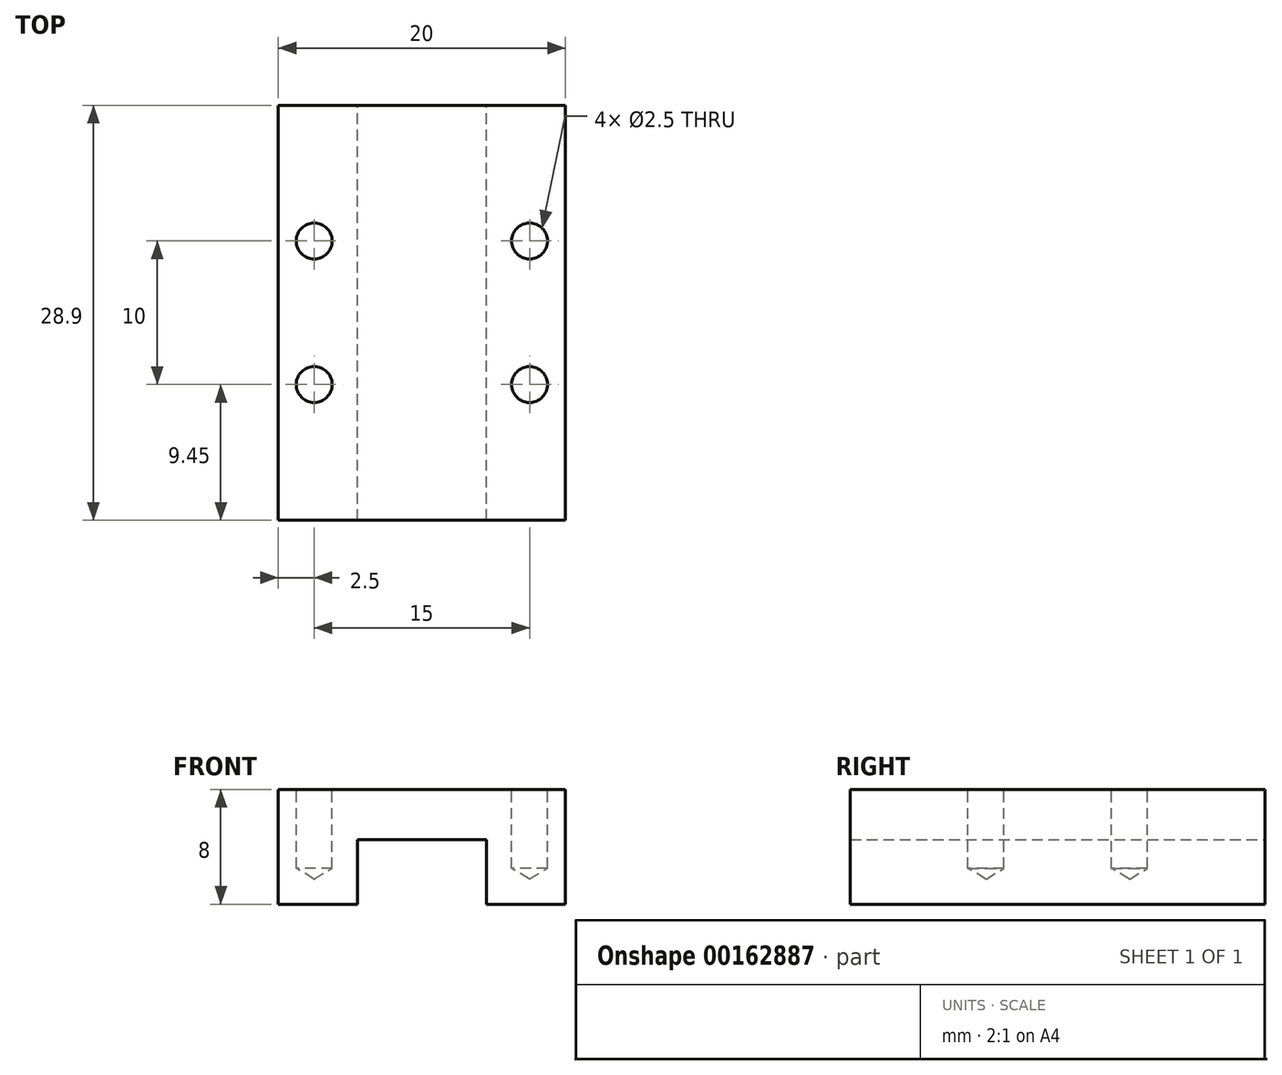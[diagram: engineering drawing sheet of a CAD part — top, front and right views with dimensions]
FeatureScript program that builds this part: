
annotation { "Feature Type Name" : "Feature", "Feature Type Description" : "" }
export const myFeature = defineFeature(function(context is Context, id is Id, definition is map)
    precondition{}
    {
        {
            var Q0;
            Q0=qCreatedBy(makeId("Front.planeOp"),FACE);
            var sketch = newSketch(context, id + "F0", { "sketchPlane" : qUnion([Q0])});
            skLineSegment(sketch, "E0", {"start": v(0, 4.05) * mm, "end": v(-10, 4.05) * mm});
            skLineSegment(sketch, "E1", {"start": v(-10, 4.05) * mm, "end": v(-10, -3.95) * mm});
            skLineSegment(sketch, "E2", {"start": v(-10, -3.95) * mm, "end": v(-4.5, -3.95) * mm});
            skLineSegment(sketch, "E3", {"start": v(-4.5, -3.95) * mm, "end": v(-4.5, 0.55) * mm});
            skLineSegment(sketch, "E4", {"start": v(-4.5, 0.55) * mm, "end": v(0, 0.55) * mm});
            skLineSegment(sketch, "E5.MirrorCS", {"start": v(4.5, -3.95) * mm, "end": v(4.5, 0.55) * mm});
            skLineSegment(sketch, "E6.MirrorCS", {"start": v(0, 4.05) * mm, "end": v(10, 4.05) * mm});
            skLineSegment(sketch, "E7.MirrorCS", {"start": v(10, -3.95) * mm, "end": v(4.5, -3.95) * mm});
            skLineSegment(sketch, "E8.MirrorCS", {"start": v(4.5, 0.55) * mm, "end": v(0, 0.55) * mm});
            skLineSegment(sketch, "E9.MirrorCS", {"start": v(10, 4.05) * mm, "end": v(10, -3.95) * mm});
            skSolve(sketch);
        }
        {
            var Q0;
            Q0=makeQuery(id+"F0.imprint","IMPRINT",FACE,{"disambiguationData":[TD([[makeQuery(id+"F0.imprint","IMPRINT",EDGE,{"derivedFrom":sQuery(id+"F0.wireOp",EDGE,"E0")}),1.0]])]});
            extrude(context, id + "F1", {"entities" : qUnion([Q0]), "depth" : 14.45 * mm, "offsetDistance" : 25 * mm, "hasSecondDirection" : true, "secondDirectionOppositeDirection" : true, "secondDirectionDepth" : 14.45 * mm});
        }
        {
            var Q0;
            Q0=makeQuery(id+"F1.opExtrude","SWEPT_FACE",FACE,{"disambiguationData":[OSD([sQuery(id+"F0.wireOp",EDGE,"E0"),sQuery(id+"F0.wireOp",EDGE,"E6.MirrorCS")])]});
            var sketch = newSketch(context, id + "F2", { "sketchPlane" : qUnion([Q0])});
            skLineSegment(sketch, "E10.bottom", {"start": v(7.5, -5) * mm, "end": v(-7.5, -5) * mm, "construction": true});
            skLineSegment(sketch, "E10.top", {"start": v(7.5, 5) * mm, "end": v(-7.5, 5) * mm, "construction": true});
            skLineSegment(sketch, "E10.left", {"start": v(7.5, -5) * mm, "end": v(7.5, 5) * mm, "construction": true});
            skLineSegment(sketch, "E10.right", {"start": v(-7.5, -5) * mm, "end": v(-7.5, 5) * mm, "construction": true});
            skPoint(sketch, "E10.middle", {"position": v(0, 0) * mm});
            skSolve(sketch);
        }
        {
            var Q0;
            Q0=sQuery(id+"F2.wireOp",VERTEX,"E10.top.end");
            var Q1;
            Q1=sQuery(id+"F2.wireOp",VERTEX,"E10.bottom.end");
            var Q2;
            Q2=sQuery(id+"F2.wireOp",VERTEX,"E10.bottom.start");
            var Q3;
            Q3=sQuery(id+"F2.wireOp",VERTEX,"E10.top.start");
            var Q4;
            Q4=makeQuery(id+"F1.opExtrude","SWEPT_BODY",BODY,{"disambiguationData":[OSD([sQuery(id+"F0.wireOp",EDGE,"E0"),sQuery(id+"F0.wireOp",EDGE,"E1"),sQuery(id+"F0.wireOp",EDGE,"E2"),sQuery(id+"F0.wireOp",EDGE,"E3"),sQuery(id+"F0.wireOp",EDGE,"E4"),sQuery(id+"F0.wireOp",EDGE,"E5.MirrorCS"),sQuery(id+"F0.wireOp",EDGE,"E6.MirrorCS"),sQuery(id+"F0.wireOp",EDGE,"E7.MirrorCS"),sQuery(id+"F0.wireOp",EDGE,"E8.MirrorCS"),sQuery(id+"F0.wireOp",EDGE,"E9.MirrorCS")])]});
            hole(context, id + "F3", {"style" : HoleStyle.SIMPLE, "endStyle" : HoleEndStyle.BLIND, "standardTappedOrClearance" : lookupTablePath({ "standard" : "ISO", "engagement" : "75%", "pitch" : "0.5 mm", "size" : "M3", "type" : "Tapped" }), "standardBlindInLast" : lookupTablePath({ "standard" : "ISO", "engagement" : "75%", "pitch" : "0.5 mm", "size" : "M3", "type" : "Tapped" }), "holeDiameter" : 2.5 * mm, "majorDiameter" : 3 * mm, "showTappedDepth" : true, "holeDepth" : 5.5 * mm, "isTappedThrough" : true, "tappedDepth" : 4 * mm, "tapClearance" : 3, "startFromSketch" : true, "locations" : qUnion([Q0, Q1, Q2, Q3]), "scope" : qUnion([Q4])});
        }
    });
